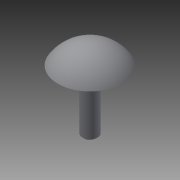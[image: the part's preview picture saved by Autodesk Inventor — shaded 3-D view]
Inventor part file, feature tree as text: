
AUTODESK INVENTOR PART (.ipt)
format: ipt  version: 2015 (Build 190159000, 159)  size: 97,792 bytes
history: native  units: in
note: dims shown in document units (in); Inventor stores cm internally (conversion verified against a paired STEP export)
features: revolve x1, chamfer x1, sketch x1
ambient origin geometry x8: Origin, YZ Plane, XZ Plane, XY Plane, X Axis, Y Axis, Z Axis, Center Point
bodies: Solid1 (feature_tree)
feature tree (3):
  revolve  "Revolution1"  [1 undecoded]
  chamfer  "Chamfer1"  Distance=0.325in
  sketch  "Sketch1"  dims[d0=0.1562in d1=0.25in d2=0.325in d3=0.0312in d4=0.1in d5=90.0deg d6=0.01in d7=0.125in d8=45.0deg]
note: 1 required parameter value undecoded (feature->parameter linkage not recoverable at this tier; creation-order binding heuristic only, values carry confidence <= 0.55)
